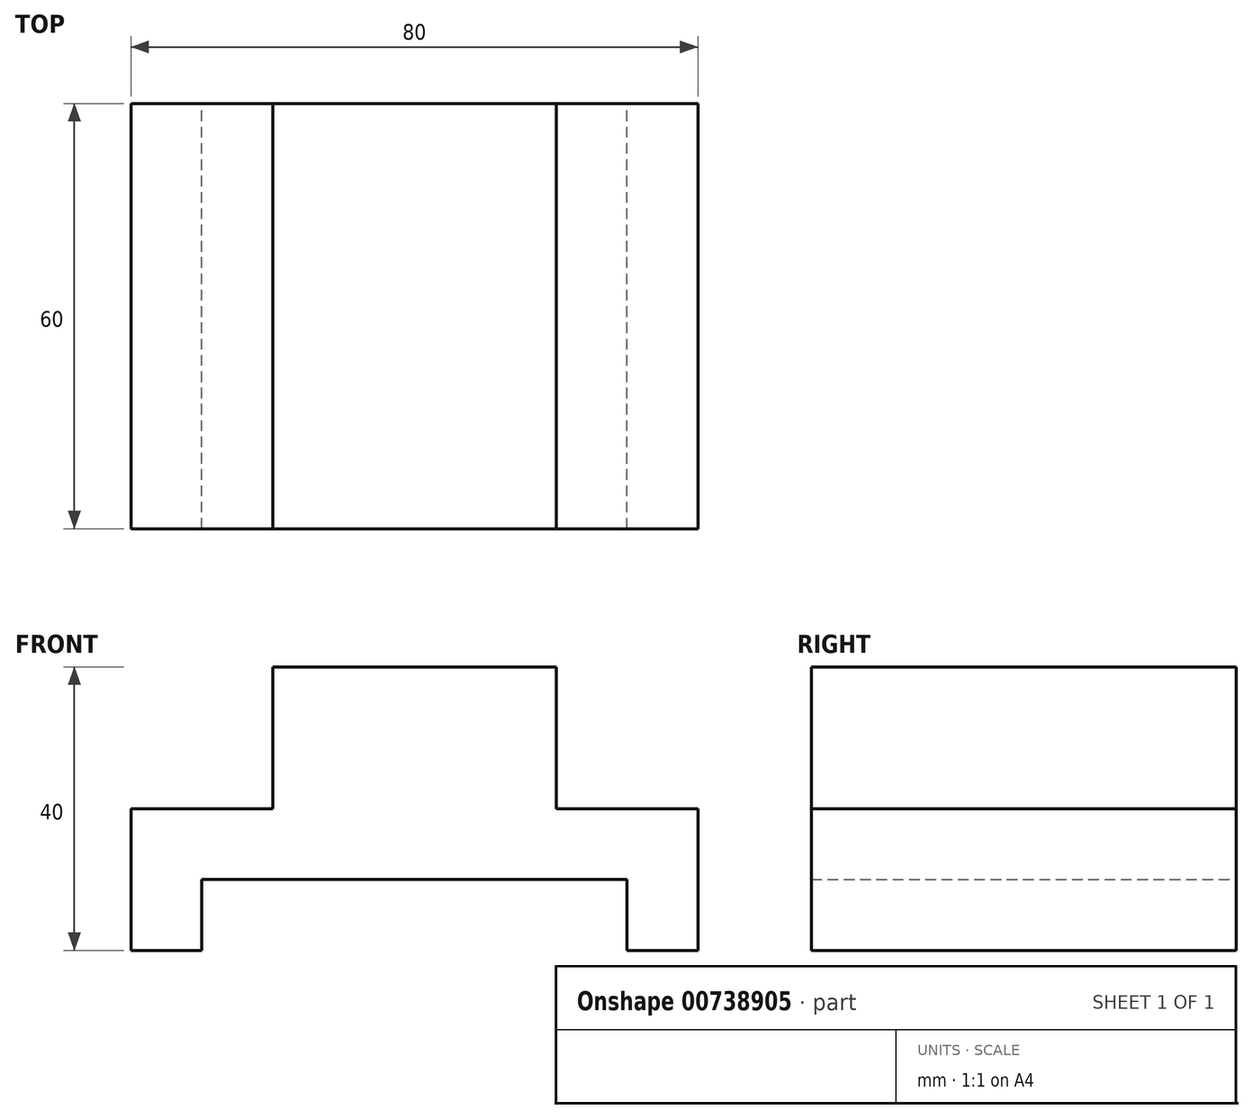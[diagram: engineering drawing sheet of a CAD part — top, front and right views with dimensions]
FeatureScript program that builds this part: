
annotation { "Feature Type Name" : "Feature", "Feature Type Description" : "" }
export const myFeature = defineFeature(function(context is Context, id is Id, definition is map)
    precondition{}
    {
        {
            var Q0;
            Q0=qCreatedBy(makeId("Front.planeOp"),FACE);
            var sketch = newSketch(context, id + "F0", { "sketchPlane" : qUnion([Q0])});
            skLineSegment(sketch, "E0", {"start": v(0, 0) * mm, "end": v(10, 0) * mm});
            skLineSegment(sketch, "E1", {"start": v(10, 0) * mm, "end": v(10, 10) * mm});
            skLineSegment(sketch, "E2", {"start": v(80, 0) * mm, "end": v(80, 20) * mm});
            skLineSegment(sketch, "E3", {"start": v(80, 20) * mm, "end": v(60, 20) * mm});
            skLineSegment(sketch, "E4", {"start": v(60, 20) * mm, "end": v(60, 40) * mm});
            skLineSegment(sketch, "E5", {"start": v(60, 40) * mm, "end": v(20, 40) * mm});
            skLineSegment(sketch, "E6", {"start": v(20, 40) * mm, "end": v(20, 20) * mm});
            skLineSegment(sketch, "E7", {"start": v(20, 20) * mm, "end": v(0, 20) * mm});
            skLineSegment(sketch, "E8", {"start": v(0, 20) * mm, "end": v(0, 0) * mm});
            skLineSegment(sketch, "E9", {"start": v(80, 0) * mm, "end": v(70, 0) * mm});
            skLineSegment(sketch, "E10", {"start": v(70, 0) * mm, "end": v(70, 10) * mm});
            skLineSegment(sketch, "E11", {"start": v(10, 10) * mm, "end": v(70, 10) * mm});
            skSolve(sketch);
        }
        {
            var Q0;
            Q0 = qSketchRegion(id + "F0", true);
            extrude(context, id + "F1", {"entities" : qUnion([Q0]), "depth" : 60 * mm, "offsetDistance" : 25 * mm});
        }
    });
